# Revit family: DBLTD_TheSenatorGroup_OfficeChairs_Colab_Seating_Ottoman_US
name_source: partatom
category: Furniture
units: mm (PartAtom-declared; Revit-internal decimal feet)

## family parameters
Always vertical = Yes
Cut with Voids When Loaded = No
OmniClass Number = 23.40.20.00
OmniClass Title = General Furniture and Specialties
Room Calculation Point = No
Shared = Yes
Work Plane-Based = No

## types (1)
- Ottoman
    Assembly Code = E2020200
    AssetType = Movable
    Category = Pr_40_50_12_57 Office chairs
    Color = Seat & Back: Fully Upholstered. Frame: Smoke Grey Powder Coat. Shelf: Available in Senator
standard 25mm MFC finishes.
    Constituents = Upholstered Seat and Back, Steel Frame
    Cost = 0 $
    Default Elevation = 0"
    Description = Ottoman
    DurationUnit = years
    ExpectedLife = 5
    Finish = Seat & Back: Fully Upholstered. Frame: Smoke Grey Powder Coat. Shelf: Available in Senator
standard 25mm MFC finishes.
    Keynote = Pr_40_50_12_57 Office chairs
    Manufacturer = The Senator Group
    ManufacturerName = The Senator Group
    ManufacturerURL = https://www.senator.online
    Material = Seat: Fully Upholstered Wood Frame Construction with Foam. Frame: Steel.
    Model = CBOT1
    ModelNumber = CBOT1
    ModelReference = Ottoman
    Name = Chair
    NominalDepth = 24"
    NominalHeight = 19"
    NominalWidth = 24"
    ProductInformation = https://www.senator.online
    SeatingHeight = 19"
    Shape = Rectangular
    Size = 24.02" x 24.02" x 19.09"
    Type Comments = Ottoman
    URL = https://www.thesenatorgroup.com
    Uniclass2015Code = Pr_40_50_12_57
    Uniclass2015Title = Office chairs
    Uniclass2015Version = Products v1.15
    Version = 1
    WarrantyDescription = Senator warrants that its manufactured products are free from manufacturing defects - in materials or workmanship - for a period of ten (10) years on Senator Seating ranges; and fifteen (15) years on Senator Desking ranges
    WarrantyDurationLabor = 5
    WarrantyDurationParts = 5
    WarrantyDurationUnit = years
    WarrantyGuarantorLabor = https://www.thesenatorgroup.com
    WarrantyGuarantorParts = https://www.thesenatorgroup.com

## geometry (parser evidence)
native form markers: Sweep x5
no freeform markers — native parametric forms only
